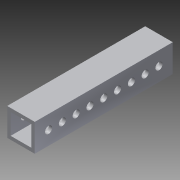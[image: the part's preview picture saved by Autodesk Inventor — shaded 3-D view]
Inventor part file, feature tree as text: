
AUTODESK INVENTOR PART (.ipt)
format: ipt  version: 2013 (Build 170138000, 138)  size: 126,464 bytes
history: native  units: in
note: dims shown in document units (in); Inventor stores cm internally (conversion verified against a paired STEP export)
features: extrude x2, sketch x1
ambient origin geometry x8: Origin, YZ Plane, XZ Plane, XY Plane, X Axis, Y Axis, Z Axis, Center Point
bodies: Solid1 (feature_tree)
feature tree (3):
  extrude  "Extrusion1"  Depth=1.0in
  extrude  "Extrusion2"  Depth=0.125in
  sketch  "Sketch1"  dims[d0=1.0in d1=1.0in d2=0.125in d3=5.0in d4=0.0in d5=0.5in d7=0.26in d8=16.5in d9=0.0in d13=5.0in d14=3.5433in d16=0.5in d17=0.3937in d19=1.0in]
